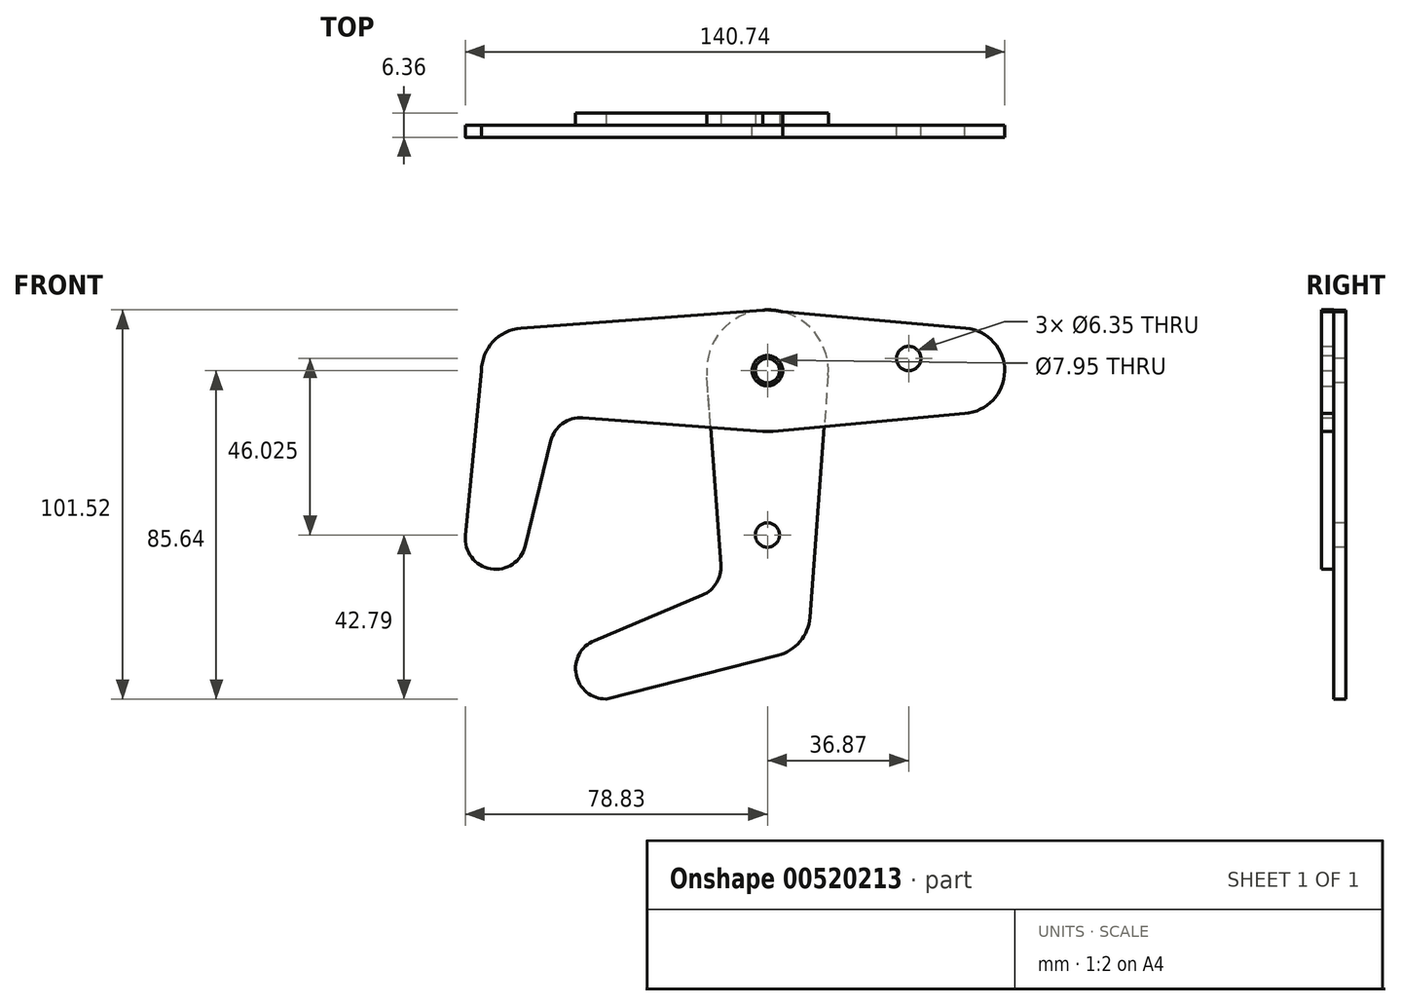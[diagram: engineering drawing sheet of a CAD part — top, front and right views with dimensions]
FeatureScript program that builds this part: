
annotation { "Feature Type Name" : "Feature", "Feature Type Description" : "" }
export const myFeature = defineFeature(function(context is Context, id is Id, definition is map)
    precondition{}
    {
        {
            var Q0;
            Q0=qCreatedBy(makeId("Front.planeOp"),FACE);
            var sketch = newSketch(context, id + "F0", { "sketchPlane" : qUnion([Q0])});
            skCircle(sketch, "E0", {"center": v(0, 33.5) * mm, "radius": 3.18 * mm});
            skCircle(sketch, "E1", {"center": v(0, 33.5) * mm, "radius": 15.88 * mm});
            skCircle(sketch, "E2", {"center": v(0, 33.5) * mm, "radius": 3.98 * mm});
            skCircle(sketch, "E3", {"center": v(-63.5, 33.5) * mm, "radius": 11.11 * mm});
            skCircle(sketch, "E4", {"center": v(-70.9, -10.34) * mm, "radius": 7.94 * mm});
            skCircle(sketch, "E5", {"center": v(50.8, 33.5) * mm, "radius": 11.11 * mm});
            skCircle(sketch, "E6", {"center": v(0, -30) * mm, "radius": 11.11 * mm});
            skCircle(sketch, "E7", {"center": v(-42.12, -44.22) * mm, "radius": 7.94 * mm});
            skCircle(sketch, "E8", {"center": v(50.8, 33.5) * mm, "radius": 3.18 * mm});
            skLineSegment(sketch, "E9", {"start": v(-63.5, 33.5) * mm, "end": v(50.8, 33.5) * mm, "construction": true});
            skLineSegment(sketch, "E10", {"start": v(-70.9, -10.34) * mm, "end": v(-63.5, 33.5) * mm, "construction": true});
            skLineSegment(sketch, "E11", {"start": v(0, 33.5) * mm, "end": v(0, -30) * mm, "construction": true});
            skLineSegment(sketch, "E12", {"start": v(-42.12, -44.22) * mm, "end": v(0, -30) * mm, "construction": true});
            skCircle(sketch, "E13", {"center": v(36.87, 36.67) * mm, "radius": 3.18 * mm});
            skCircle(sketch, "E14", {"center": v(-70.9, -10.34) * mm, "radius": 3.18 * mm});
            skCircle(sketch, "E15", {"center": v(-63.5, 33.5) * mm, "radius": 3.18 * mm});
            skCircle(sketch, "E16", {"center": v(0, -30) * mm, "radius": 3.18 * mm});
            skCircle(sketch, "E17", {"center": v(-42.12, -44.22) * mm, "radius": 3.18 * mm});
            skLineSegment(sketch, "E18", {"start": v(-42.12, -52.15) * mm, "end": v(2.73, -40.78) * mm});
            skLineSegment(sketch, "E19", {"start": v(15.83, 32.3) * mm, "end": v(11.08, -30.84) * mm});
            skLineSegment(sketch, "E20", {"start": v(51.5, 22.4) * mm, "end": v(0, 17.54) * mm});
            skLineSegment(sketch, "E21", {"start": v(-1.2, 49.32) * mm, "end": v(51.8, 44.56) * mm});
            skLineSegment(sketch, "E22", {"start": v(-64.33, 44.57) * mm, "end": v(-1.2, 49.32) * mm});
            skLineSegment(sketch, "E23", {"start": v(-74.61, 33.5) * mm, "end": v(-78.8, -9.57) * mm});
            skLineSegment(sketch, "E24.trimOffspring", {"start": v(-64.34, 22.4) * mm, "end": v(-65.36, 22.49) * mm});
            skPoint(sketch, "E25.second.point", {"position": v(-55, 10.82) * mm});
            skPoint(sketch, "E25.third.point", {"position": v(-36.95, 12.34) * mm});
            skLineSegment(sketch, "E26", {"start": v(-1.2, 17.66) * mm, "end": v(-48.2, 21.2) * mm});
            skLineSegment(sketch, "E27", {"start": v(-56.53, 15.15) * mm, "end": v(-63.18, -12.22) * mm});
            skArc(sketch, "E28.filletArc", {"start": v(-48.2, 21.2) * mm, "mid": v(-53.48, 19.7) * mm, "end": v(-56.53, 15.15) * mm});
            skCircle(sketch, "E29", {"center": v(0, -9.36) * mm, "radius": 3.18 * mm});
            skLineSegment(sketch, "E30", {"start": v(-45.19, -36.9) * mm, "end": v(-16.97, -25.07) * mm});
            skLineSegment(sketch, "E31", {"start": v(-12.11, -17.14) * mm, "end": v(-15.83, 32.3) * mm});
            skPoint(sketch, "E32.visualSharp", {"position": v(-11.68, -22.86) * mm});
            skArc(sketch, "E32.filletArc", {"start": v(-16.97, -25.07) * mm, "mid": v(-13.26, -21.9) * mm, "end": v(-12.11, -17.14) * mm});
            skLineSegment(sketch, "E33", {"start": v(-70.9, -10.34) * mm, "end": v(-42.12, -44.22) * mm, "construction": true});
            skSolve(sketch);
        }
        {
            var Q0;
            Q0=makeQuery(id+"F0.imprint","IMPRINT",FACE,{"disambiguationData":[TD([[makeQuery(id+"F0.imprint","IMPRINT",EDGE,{"derivedFrom":sQuery(id+"F0.wireOp",EDGE,"E14")}),1.0]])]});
            var Q1;
            Q1=makeQuery(id+"F0.imprint","IMPRINT",FACE,{"disambiguationData":[TD([[makeQuery(id+"F0.imprint","IMPRINT",EDGE,{"derivedFrom":sQuery(id+"F0.wireOp",EDGE,"E15")}),1.0]])]});
            var Q2;
            Q2=makeQuery(id+"F0.imprint","IMPRINT",FACE,{"disambiguationData":[TD([[makeQuery(id+"F0.imprint","IMPRINT",EDGE,{"derivedFrom":sQuery(id+"F0.wireOp",EDGE,"E15")}),-1.0]])]});
            var Q3;
            Q3=makeQuery(id+"F0.imprint","IMPRINT",FACE,{"disambiguationData":[TD([[makeQuery(id+"F0.imprint","IMPRINT",EDGE,{"derivedFrom":sQuery(id+"F0.wireOp",EDGE,"E14")}),-1.0]])]});
            var Q4;
            Q4=makeQuery(id+"F0.imprint","IMPRINT",FACE,{"disambiguationData":[TD([[makeQuery(id+"F0.imprint","IMPRINT",EDGE,{"derivedFrom":sQuery(id+"F0.wireOp",EDGE,"E8")}),-1.0]])]});
            var Q5;
            {var subQ0=sQuery(id+"F0.wireOp",EDGE,"E13");Q5=makeQuery(id+"F0.imprint","IMPRINT",FACE,{"disambiguationData":[TD([[makeQuery(id+"F0.imprint","IMPRINT",EDGE,{"derivedFrom":subQ0}),-1.0]])]});}
            var Q6;
            Q6=makeQuery(id+"F0.imprint","IMPRINT",FACE,{"disambiguationData":[TD([[makeQuery(id+"F0.imprint","IMPRINT",EDGE,{"derivedFrom":sQuery(id+"F0.wireOp",EDGE,"E8")}),1.0]])]});
            var Q7;
            Q7=makeQuery(id+"F0.imprint","IMPRINT",FACE,{"disambiguationData":[TD([[makeQuery(id+"F0.imprint","IMPRINT",EDGE,{"derivedFrom":sQuery(id+"F0.wireOp",EDGE,"E13")}),1.0]])]});
            var Q8;
            {var subQ0=sQuery(id+"F0.wireOp",EDGE,"E21");var subQ1=sQuery(id+"F0.wireOp",EDGE,"E1");var subQ3=makeQuery(id+"F0.imprint","INTERSECT",VERTEX,{"derivedFrom":[subQ1,subQ0]});Q8=makeQuery(id+"F0.imprint","IMPRINT",FACE,{"disambiguationData":[TD([[makeQuery(id+"F0.imprint","IMPRINT",EDGE,{"disambiguationData":[TD([[subQ3,-1.0]])],"derivedFrom":subQ1}),1.0]])]});}
            var Q9;
            {var subQ0=sQuery(id+"F0.wireOp",EDGE,"E22");Q9=makeQuery(id+"F0.imprint","IMPRINT",FACE,{"disambiguationData":[TD([[makeQuery(id+"F0.imprint","IMPRINT",EDGE,{"derivedFrom":subQ0}),-1.0]])]});}
            var Q10;
            Q10=makeQuery(id+"F0.imprint","IMPRINT",FACE,{"disambiguationData":[TD([[makeQuery(id+"F0.imprint","IMPRINT",EDGE,{"derivedFrom":sQuery(id+"F0.wireOp",EDGE,"E2")}),-1.0]])]});
            var Q11;
            {var subQ0=sQuery(id+"F0.wireOp",EDGE,"E26");var subQ1=sQuery(id+"F0.wireOp",EDGE,"E1");var subQ2=makeQuery(id+"F0.imprint","INTERSECT",VERTEX,{"derivedFrom":[subQ1,subQ0]});Q11=makeQuery(id+"F0.imprint","IMPRINT",FACE,{"disambiguationData":[TD([[makeQuery(id+"F0.imprint","IMPRINT",EDGE,{"disambiguationData":[TD([[subQ2,1.0]])],"derivedFrom":subQ1}),-1.0]])]});}
            var Q12;
            {var subQ0=sQuery(id+"F0.wireOp",EDGE,"E19");var subQ1=sQuery(id+"F0.wireOp",EDGE,"E1");var subQ2=makeQuery(id+"F0.imprint","INTERSECT",VERTEX,{"derivedFrom":[subQ1,subQ0]});Q12=makeQuery(id+"F0.imprint","IMPRINT",FACE,{"disambiguationData":[TD([[makeQuery(id+"F0.imprint","IMPRINT",EDGE,{"disambiguationData":[TD([[subQ2,1.0]])],"derivedFrom":subQ1}),-1.0]])]});}
            extrude(context, id + "F1", {"entities" : qUnion([Q0, Q1, Q2, Q3, Q4, Q5, Q6, Q7, Q8, Q9, Q10, Q11, Q12]), "depth" : 3.17 * mm, "offsetDistance" : 25.4 * mm});
        }
        {
            var Q0;
            Q0=makeQuery(id+"F0.imprint","IMPRINT",FACE,{"disambiguationData":[TD([[makeQuery(id+"F0.imprint","IMPRINT",EDGE,{"derivedFrom":sQuery(id+"F0.wireOp",EDGE,"E2")}),-1.0]])]});
            var Q1;
            Q1=makeQuery(id+"F0.imprint","IMPRINT",FACE,{"disambiguationData":[TD([[makeQuery(id+"F0.imprint","IMPRINT",EDGE,{"derivedFrom":sQuery(id+"F0.wireOp",EDGE,"E29")}),-1.0]])]});
            var Q2;
            Q2=makeQuery(id+"F0.imprint","IMPRINT",FACE,{"disambiguationData":[TD([[makeQuery(id+"F0.imprint","IMPRINT",EDGE,{"derivedFrom":sQuery(id+"F0.wireOp",EDGE,"E16")}),-1.0]])]});
            var Q3;
            Q3=makeQuery(id+"F0.imprint","IMPRINT",FACE,{"disambiguationData":[TD([[makeQuery(id+"F0.imprint","IMPRINT",EDGE,{"derivedFrom":sQuery(id+"F0.wireOp",EDGE,"E16")}),1.0]])]});
            var Q4;
            Q4=makeQuery(id+"F0.imprint","IMPRINT",FACE,{"disambiguationData":[TD([[makeQuery(id+"F0.imprint","IMPRINT",EDGE,{"derivedFrom":sQuery(id+"F0.wireOp",EDGE,"E17")}),1.0]])]});
            var Q5;
            Q5=makeQuery(id+"F0.imprint","IMPRINT",FACE,{"disambiguationData":[TD([[makeQuery(id+"F0.imprint","IMPRINT",EDGE,{"derivedFrom":sQuery(id+"F0.wireOp",EDGE,"E17")}),-1.0]])]});
            var Q6;
            Q6=makeQuery(id+"F0.imprint","IMPRINT",FACE,{"disambiguationData":[TD([[makeQuery(id+"F0.imprint","IMPRINT",EDGE,{"derivedFrom":sQuery(id+"F0.wireOp",EDGE,"E29")}),1.0]])]});
            var Q7;
            Q7=makeQuery(id+"F0.imprint","IMPRINT",FACE,{"disambiguationData":[TD([[makeQuery(id+"F0.imprint","IMPRINT",EDGE,{"derivedFrom":sQuery(id+"F0.wireOp",EDGE,"E0")}),-1.0]])]});
            var Q8;
            {var subQ0=sQuery(id+"F0.wireOp",EDGE,"E19");var subQ1=sQuery(id+"F0.wireOp",EDGE,"E1");var subQ2=makeQuery(id+"F0.imprint","INTERSECT",VERTEX,{"derivedFrom":[subQ1,subQ0]});Q8=makeQuery(id+"F0.imprint","IMPRINT",FACE,{"disambiguationData":[TD([[makeQuery(id+"F0.imprint","IMPRINT",EDGE,{"disambiguationData":[TD([[subQ2,1.0]])],"derivedFrom":subQ1}),-1.0]])]});}
            var Q9;
            {var subQ0=sQuery(id+"F0.wireOp",EDGE,"E26");var subQ1=sQuery(id+"F0.wireOp",EDGE,"E1");var subQ2=makeQuery(id+"F0.imprint","INTERSECT",VERTEX,{"derivedFrom":[subQ1,subQ0]});Q9=makeQuery(id+"F0.imprint","IMPRINT",FACE,{"disambiguationData":[TD([[makeQuery(id+"F0.imprint","IMPRINT",EDGE,{"disambiguationData":[TD([[subQ2,1.0]])],"derivedFrom":subQ1}),-1.0]])]});}
            extrude(context, id + "F2", {"entities" : qUnion([Q0, Q1, Q2, Q3, Q4, Q5, Q6, Q7, Q8, Q9]), "oppositeDirection" : true, "depth" : 3.17 * mm, "offsetDistance" : 25.4 * mm});
        }
        {
            var Q0;
            Q0=makeQuery(id+"F0.imprint","IMPRINT",FACE,{"disambiguationData":[TD([[makeQuery(id+"F0.imprint","IMPRINT",EDGE,{"derivedFrom":sQuery(id+"F0.wireOp",EDGE,"E13")}),1.0]])]});
            var Q1;
            Q1=makeQuery(id+"F0.imprint","IMPRINT",FACE,{"disambiguationData":[TD([[makeQuery(id+"F0.imprint","IMPRINT",EDGE,{"derivedFrom":sQuery(id+"F0.wireOp",EDGE,"E29")}),1.0]])]});
            extrude(context, id + "F3", {"entities" : qUnion([Q0, Q1]), "operationType" : NewBodyOperationType.REMOVE, "depth" : 25.4 * mm, "offsetDistance" : 25.4 * mm});
        }
        {
            var Q0;
            Q0=makeQuery(id+"F0.imprint","IMPRINT",FACE,{"disambiguationData":[TD([[makeQuery(id+"F0.imprint","IMPRINT",EDGE,{"derivedFrom":sQuery(id+"F0.wireOp",EDGE,"E29")}),1.0]])]});
            var Q1;
            Q1=sQuery(id+"F0.wireOp",EDGE,"E16");
            extrude(context, id + "F4", {"entities" : qUnion([Q0]), "operationType" : NewBodyOperationType.REMOVE, "surfaceEntities" : qUnion([Q1]), "oppositeDirection" : true, "depth" : 25.4 * mm, "offsetDistance" : 25.4 * mm});
        }
    });
